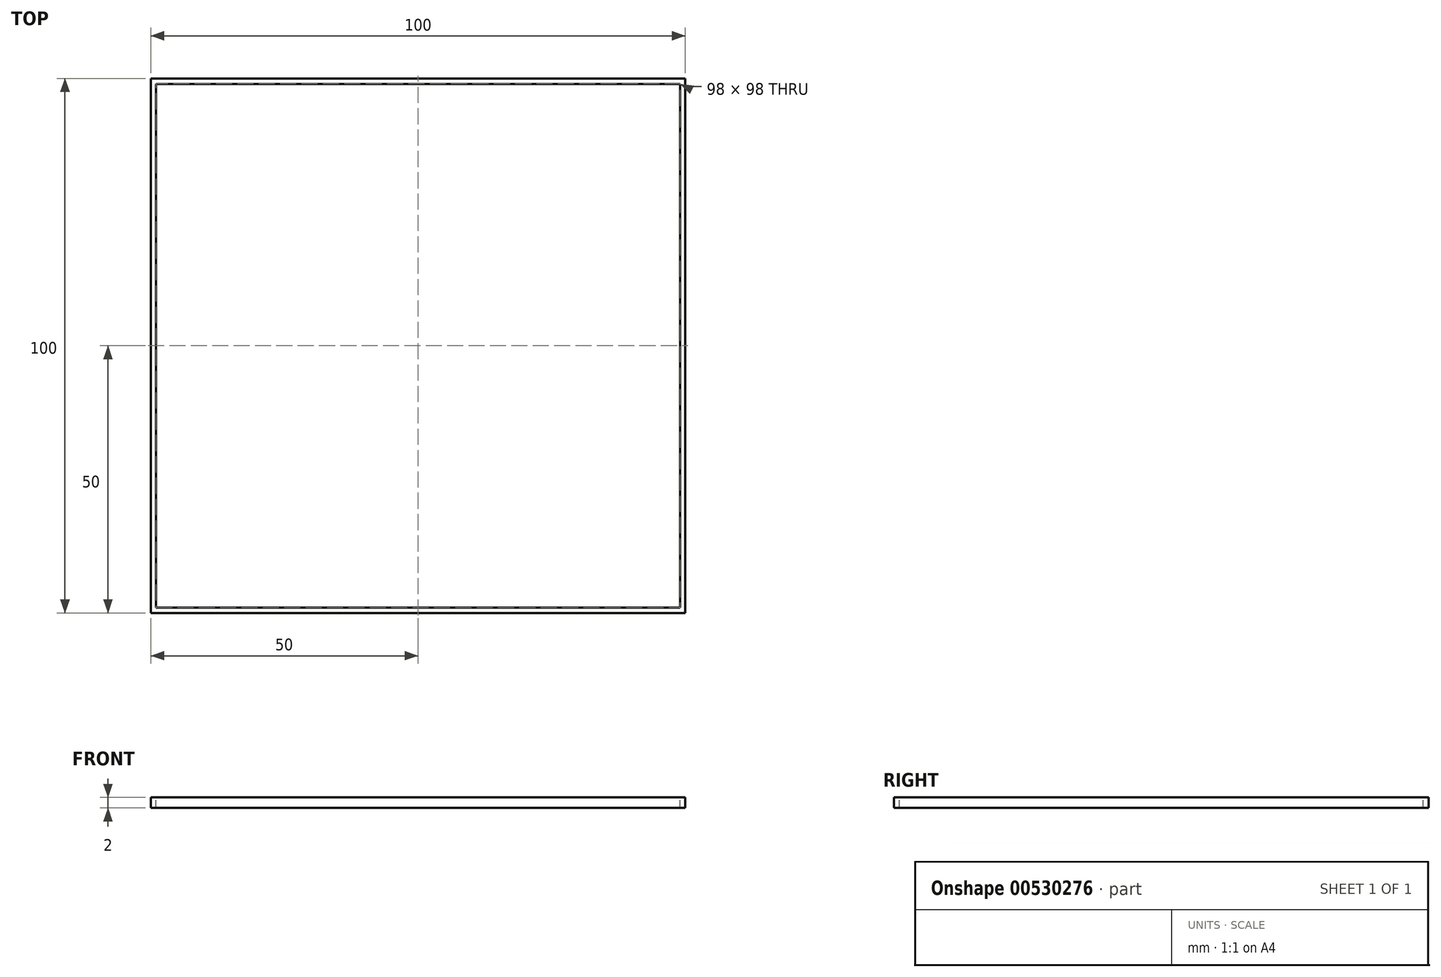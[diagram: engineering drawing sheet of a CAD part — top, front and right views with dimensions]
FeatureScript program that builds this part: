
annotation { "Feature Type Name" : "Feature", "Feature Type Description" : "" }
export const myFeature = defineFeature(function(context is Context, id is Id, definition is map)
    precondition{}
    {
        {
            var Q0;
            Q0=qCreatedBy(makeId("Top.planeOp"),FACE);
            var sketch = newSketch(context, id + "F0", { "sketchPlane" : qUnion([Q0])});
            skLineSegment(sketch, "E0.bottom", {"start": v(-50, 50) * mm, "end": v(50, 50) * mm});
            skLineSegment(sketch, "E0.top", {"start": v(-50, -50) * mm, "end": v(50, -50) * mm});
            skLineSegment(sketch, "E0.left", {"start": v(-50, 50) * mm, "end": v(-50, -50) * mm});
            skLineSegment(sketch, "E0.right", {"start": v(50, 50) * mm, "end": v(50, -50) * mm});
            skSolve(sketch);
        }
        {
            var Q0;
            Q0=qSketchRegion(id+"F0",true);
            extrude(context, id + "F1", {"entities" : qUnion([Q0]), "depth" : 2 * mm, "offsetDistance" : 25 * mm});
        }
        {
            var Q0;
            Q0=makeQuery(id+"F1.opExtrude","CAP_FACE",FACE,{"disambiguationData":[OSD([sQuery(id+"F0.wireOp",EDGE,"E0.bottom"),sQuery(id+"F0.wireOp",EDGE,"E0.top"),sQuery(id+"F0.wireOp",EDGE,"E0.left"),sQuery(id+"F0.wireOp",EDGE,"E0.right")])],"isStart":false});
            var sketch = newSketch(context, id + "F2", { "sketchPlane" : qUnion([Q0])});
            skLineSegment(sketch, "E1.bottom", {"start": v(-49, 49) * mm, "end": v(49, 49) * mm});
            skLineSegment(sketch, "E1.top", {"start": v(-49, -49) * mm, "end": v(49, -49) * mm});
            skLineSegment(sketch, "E1.left", {"start": v(-49, 49) * mm, "end": v(-49, -49) * mm});
            skLineSegment(sketch, "E1.right", {"start": v(49, 49) * mm, "end": v(49, -49) * mm});
            skSolve(sketch);
        }
        {
            var Q0;
            Q0=makeQuery(id+"F2.imprint","IMPRINT",FACE,{"disambiguationData":[TD([[makeQuery(id+"F2.imprint","IMPRINT",EDGE,{"derivedFrom":sQuery(id+"F2.wireOp",EDGE,"E1.bottom")}),-1.0]])]});
            extrude(context, id + "F3", {"entities" : qUnion([Q0]), "operationType" : NewBodyOperationType.REMOVE, "oppositeDirection" : true, "depth" : 2 * mm, "offsetDistance" : 25 * mm});
        }
    });
